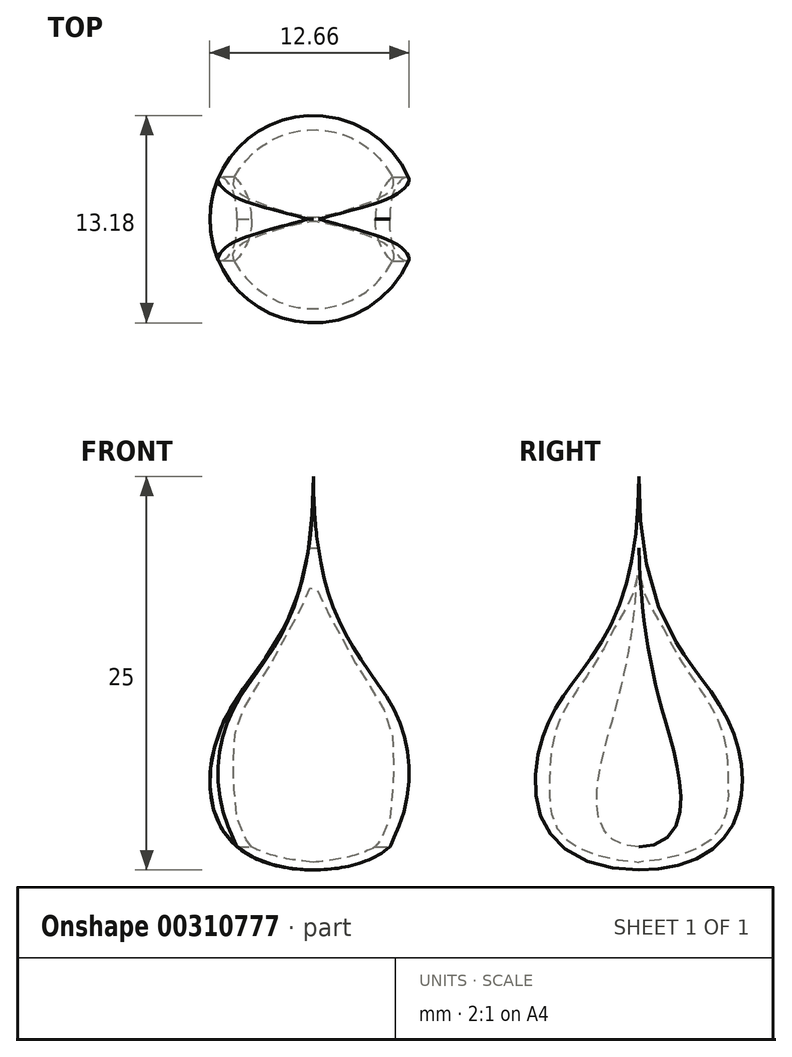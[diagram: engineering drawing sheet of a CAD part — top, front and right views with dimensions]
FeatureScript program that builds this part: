
annotation { "Feature Type Name" : "Feature", "Feature Type Description" : "" }
export const myFeature = defineFeature(function(context is Context, id is Id, definition is map)
    precondition{}
    {
        {
            var Q0;
            Q0=qCreatedBy(makeId("Front.planeOp"),FACE);
            var sketch = newSketch(context, id + "F0", { "sketchPlane" : qUnion([Q0])});
            skLineSegment(sketch, "E0", {"start": v(0, -8.55) * mm, "end": v(0, 16.45) * mm, "construction": true});
            skFitSpline(sketch, "E1", {"points": [v(0, -8.55) * mm, v(-5.9, 0.45) * mm, v(0, 16.45) * mm], "startDerivative": vector(-48.4, 0.6) * mm, "endDerivative": vector(0, 57.5) * mm});
            skLineSegment(sketch, "E2", {"start": v(0, -8.55) * mm, "end": v(0, -8.05) * mm});
            skFitSpline(sketch, "E3", {"points": [v(0, -8.05) * mm, v(-5.68, -3.3) * mm, v(-5.37, 0) * mm, v(-4.37, 2.18) * mm, v(-2.52, 5) * mm, v(-1.3, 7.26) * mm, v(0, 11.45) * mm], "startDerivative": vector(-72.06, 5.7) * mm, "endDerivative": vector(0, 40.1) * mm});
            skLineSegment(sketch, "E4", {"start": v(0, 16.45) * mm, "end": v(0, 11.45) * mm});
            skSolve(sketch);
        }
        {
            var Q0;
            Q0 = qSketchRegion(id + "F0", true);
            var Q1;
            Q1=sQuery(id+"F0.wireOp",EDGE,"E0");
            revolve(context, id + "F1", {"entities" : qUnion([Q0]), "axis" : qUnion([Q1]), "revolveType" : RevolveType.FULL});
        }
        {
            var Q0;
            Q0=qCreatedBy(makeId("Right.planeOp"),FACE);
            var sketch = newSketch(context, id + "F2", { "sketchPlane" : qUnion([Q0])});
            skLineSegment(sketch, "E5", {"start": v(0, -7.08) * mm, "end": v(0, 11.9) * mm, "construction": true});
            skFitSpline(sketch, "E6", {"points": [v(0, 11.9) * mm, v(-2.5, -2.33) * mm, v(0, -7.08) * mm], "startDerivative": vector(-1.36, -40.05) * mm, "endDerivative": vector(22.75, -0.33) * mm});
            skFitSpline(sketch, "E7.MirrorCS", {"points": [v(0, 11.9) * mm, v(2.5, -2.33) * mm, v(0, -7.08) * mm], "startDerivative": vector(1.36, -40.05) * mm, "endDerivative": vector(-22.75, -0.33) * mm});
            skSolve(sketch);
        }
        {
            var Q0;
            Q0=makeQuery(id+"F2.imprint","IMPRINT",FACE,{"disambiguationData":[TD([[makeQuery(id+"F2.imprint","IMPRINT",EDGE,{"derivedFrom":sQuery(id+"F2.wireOp",EDGE,"E6")}),1.0]])]});
            extrude(context, id + "F3", {"entities" : qUnion([Q0]), "operationType" : NewBodyOperationType.REMOVE, "endBound" : BoundingType.SYMMETRIC, "oppositeDirection" : true, "depth" : 25 * mm});
        }
    });
